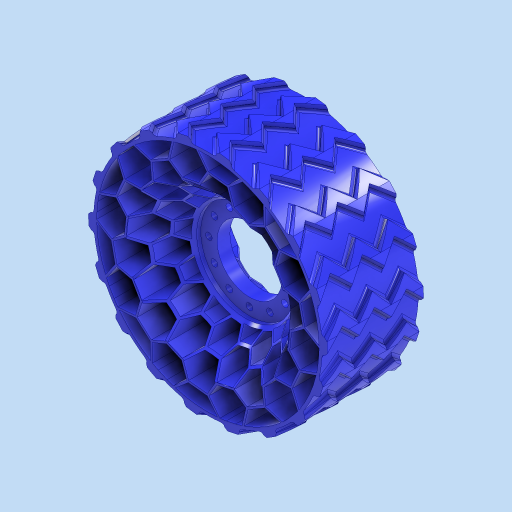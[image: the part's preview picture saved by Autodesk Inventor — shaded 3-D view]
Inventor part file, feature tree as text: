
AUTODESK INVENTOR PART (.ipt)
format: ipt  version: 2023 (Build 270158000, 158)  size: 2,894,848 bytes
history: native  units: in
note: dims shown in document units (in); Inventor stores cm internally (conversion verified against a paired STEP export)
features: extrude x21, thicken_offset x17, other x17, sketch x5, pattern_circular x2, plane x2, fillet x2, chamfer x2, mirror x1, sweep x1, projected_geometry x1
ambient origin geometry x8: Origin, YZ Plane, XZ Plane, XY Plane, X Axis, Y Axis, Z Axis, Center Point
bodies: Solid1 (feature_tree)
feature tree (71):
  sketch  "Sketch1"  dims[d0=2.9528in d1=0.0in d2=2.9528in d3=0.0in]
  extrude  "Extrusion1"  Depth=2.9528in TaperAngle=0.0deg
  thicken_offset  "Thicken1"
  thicken_offset  "Thicken2"
  thicken_offset  "Thicken3"
  thicken_offset  "Thicken4"
  thicken_offset  "Thicken5"
  thicken_offset  "Thicken6"
  thicken_offset  "Thicken7"
  thicken_offset  "Thicken8"
  thicken_offset  "Thicken9"
  thicken_offset  "Thicken10"
  thicken_offset  "Thicken11"
  thicken_offset  "Thicken12"
  thicken_offset  "Thicken13"
  thicken_offset  "Thicken14"
  thicken_offset  "Thicken15"
  thicken_offset  "Thicken16"
  thicken_offset  "Thicken17"
  pattern_circular  "Circular Pattern1"  [2 undecoded]
  sketch  "Sketch2"  dims[d4=0.0945in]
  extrude  "Extrusion2"  Depth=2.9528in TaperAngle=0.0deg
  extrude  "Extrusion3"  Depth=0.063in
  plane  "Work Plane1"
  mirror  "Mirror1"
  plane  "Work Plane2"
  sweep  "Sweep1"
  extrude  "Extrusion4"  Depth=0.063in
  fillet  "Fillet2"  Radius=2.9528in
  pattern_circular  "Circular Pattern2"  [2 undecoded]
  fillet  "Fillet1"  Radius=2.9528in
  chamfer  "Chamfer1"  Distance=0.063in
  chamfer  "Chamfer2"  Distance=2.9528in
  other  "Srf1"
  other  "Srf2"
  other  "Srf3"
  other  "Srf4"
  other  "Srf5"
  other  "Srf6"
  other  "Srf7"
  other  "Srf8"
  other  "Srf9"
  other  "Srf10"
  other  "Srf11"
  other  "Srf12"
  other  "Srf13"
  other  "Srf14"
  other  "Srf15"
  other  "Srf16"
  other  "Srf17"
  sketch  "Sketch3"  dims[d5=2.9528in d6=0.0in]
  sketch  "Sketch4"  dims[d7=0.063in]
  projected_geometry  "Projected Loop1"
  sketch  "Sketch5"  dims[d8=2.9528in d9=0.0in d10=0.063in d11=2.9528in d12=0.0in d13=0.063in d14=2.9528in d15=0.0in d16=0.063in d17=2.9528in d18=0.0in d19=0.063in d20=2.9528in d21=0.0in d22=0.063in d23=2.9528in d24=0.0in d25=0.063in d26=2.9528in d27=0.0in d28=0.063in d29=2.9528in d30=0.0in d31=0.063in d32=2.9528in d33=0.0in d34=0.063in d35=2.9528in d36=0.0in d37=0.063in d38=2.9528in d39=0.0in d40=0.063in d41=2.9528in d42=0.0in d43=0.063in d44=2.9528in d45=0.0in d46=0.063in d47=2.9528in d48=0.0in d49=0.063in d50=2.9528in d51=0.0in d52=0.063in d53=3.937in d54=360.0deg d57=4.7244in d58=2.5in d59=0.2057in d60=360.0deg d61=0.5in d62=3.0in d63=0.5in d64=0.0in d65=0.0in d66=1.2795in d67=0.0in d69=0.4724in d70=0.1575in d71=0.0787in d72=0.0787in d73=0.0787in d74=0.0787in d75=0.0in d76=0.0in d77=0.0in d78=0.0in d79=7.0866in d80=360.0deg d82=0.0039in d83=1.378in d84=1.0039in d85=1.1545in d86=45.0deg d87=1.0039in d88=1.1545in d89=45.0deg d90=0.0787in]
  extrude  "ExtrusionSrf1"  Depth=0.063in
  extrude  "ExtrusionSrf2"  Depth=2.9528in TaperAngle=0.0deg
  extrude  "ExtrusionSrf3"  Depth=0.063in
  extrude  "ExtrusionSrf4"  Depth=2.9528in TaperAngle=0.0deg
  extrude  "ExtrusionSrf5"  Depth=0.063in
  extrude  "ExtrusionSrf6"  Depth=2.9528in TaperAngle=0.0deg
  extrude  "ExtrusionSrf7"  Depth=0.063in
  extrude  "ExtrusionSrf8"  Depth=2.9528in TaperAngle=0.0deg
  extrude  "ExtrusionSrf9"  Depth=0.063in
  extrude  "ExtrusionSrf10"  Depth=2.9528in TaperAngle=0.0deg
  extrude  "ExtrusionSrf11"  Depth=0.063in
  extrude  "ExtrusionSrf12"  Depth=2.9528in TaperAngle=0.0deg
  extrude  "ExtrusionSrf13"  Depth=0.063in
  extrude  "ExtrusionSrf14"  Depth=2.9528in TaperAngle=0.0deg
  extrude  "ExtrusionSrf15"  Depth=0.063in
  extrude  "ExtrusionSrf16"  Depth=2.9528in TaperAngle=0.0deg
  extrude  "ExtrusionSrf17"  Depth=0.063in
note: 4 required parameter values undecoded (feature->parameter linkage not recoverable at this tier; creation-order binding heuristic only, values carry confidence <= 0.55)
